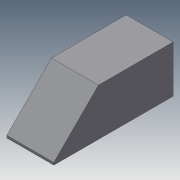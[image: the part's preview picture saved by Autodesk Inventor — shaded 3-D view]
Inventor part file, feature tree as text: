
AUTODESK INVENTOR PART (.ipt)
format: ipt  version: 2020.3 (Build 243373000, 373)  size: 90,112 bytes
history: native  units: in
note: dims shown in document units (in); Inventor stores cm internally (conversion verified against a paired STEP export)
features: extrude x1, chamfer x1, sketch x1
ambient origin geometry x8: Origin, YZ Plane, XZ Plane, XY Plane, X Axis, Y Axis, Z Axis, Center Point
bodies: Solid1 (feature_tree)
feature tree (3):
  extrude  "Extrusion1"  Depth=0.3937in
  chamfer  "Chamfer1"  Distance=1.0in
  sketch  "Sketch1"  dims[d0=0.3937in d1=0.3937in d2=1.0in d3=0.0in d4=0.374in d5=0.125in d6=45.0deg]
